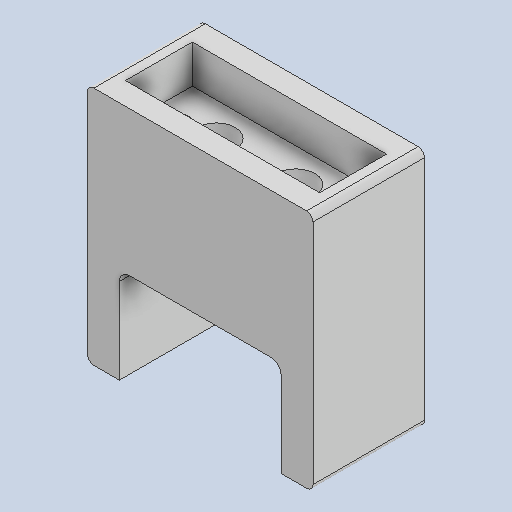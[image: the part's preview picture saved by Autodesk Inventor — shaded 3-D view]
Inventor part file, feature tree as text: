
AUTODESK INVENTOR PART (.ipt)
format: ipt  version: 2023 (Build 270158000, 158)  size: 214,016 bytes
history: native  units: in
note: dims shown in document units (in); Inventor stores cm internally (conversion verified against a paired STEP export)
features: extrude x6, sketch x5, fillet x2
ambient origin geometry x8: Origin, YZ Plane, XZ Plane, XY Plane, X Axis, Y Axis, Z Axis, Center Point
bodies: Solid1 (feature_tree)
feature tree (13):
  sketch  "Sketch1"  dims[d0=0.7874in d1=2.3622in]
  extrude  "Extrusion1"  Depth=2.3622in
  extrude  "Extrusion2"  Depth=0.0197in
  extrude  "Extrusion3"  Depth=0.0197in
  extrude  "Extrusion4"  Depth=1.811in
  extrude  "Extrusion5"  Depth=1.378in
  extrude  "Extrusion6"  Depth=0.3937in TaperAngle=0.0deg
  fillet  "Fillet1"  Radius=1.3937in
  fillet  "Fillet2"  Radius=0.3937in
  sketch  "Sketch2"  dims[d2=0.0197in d3=0.0197in]
  sketch  "Sketch3"  dims[d4=0.0197in d5=0.0197in]
  sketch  "Sketch4"  dims[d6=0.1417in d7=1.811in]
  sketch  "Sketch5"  dims[d9=2.7874in d10=1.378in d11=0.3937in d12=0.0in d13=1.3937in d14=0.0in d15=0.3937in d16=0.0787in d17=0.0in d18=0.0in d19=0.3937in d20=1.1969in d21=0.0in d22=0.0in d23=2.0in d24=0.125in d25=0.3937in d26=1.1811in d27=0.3937in d28=0.0in d29=0.2362in d30=0.9843in d31=0.3937in d32=0.0in d34=0.4724in d35=0.3937in d36=0.0in d37=0.0787in d38=0.0787in]
